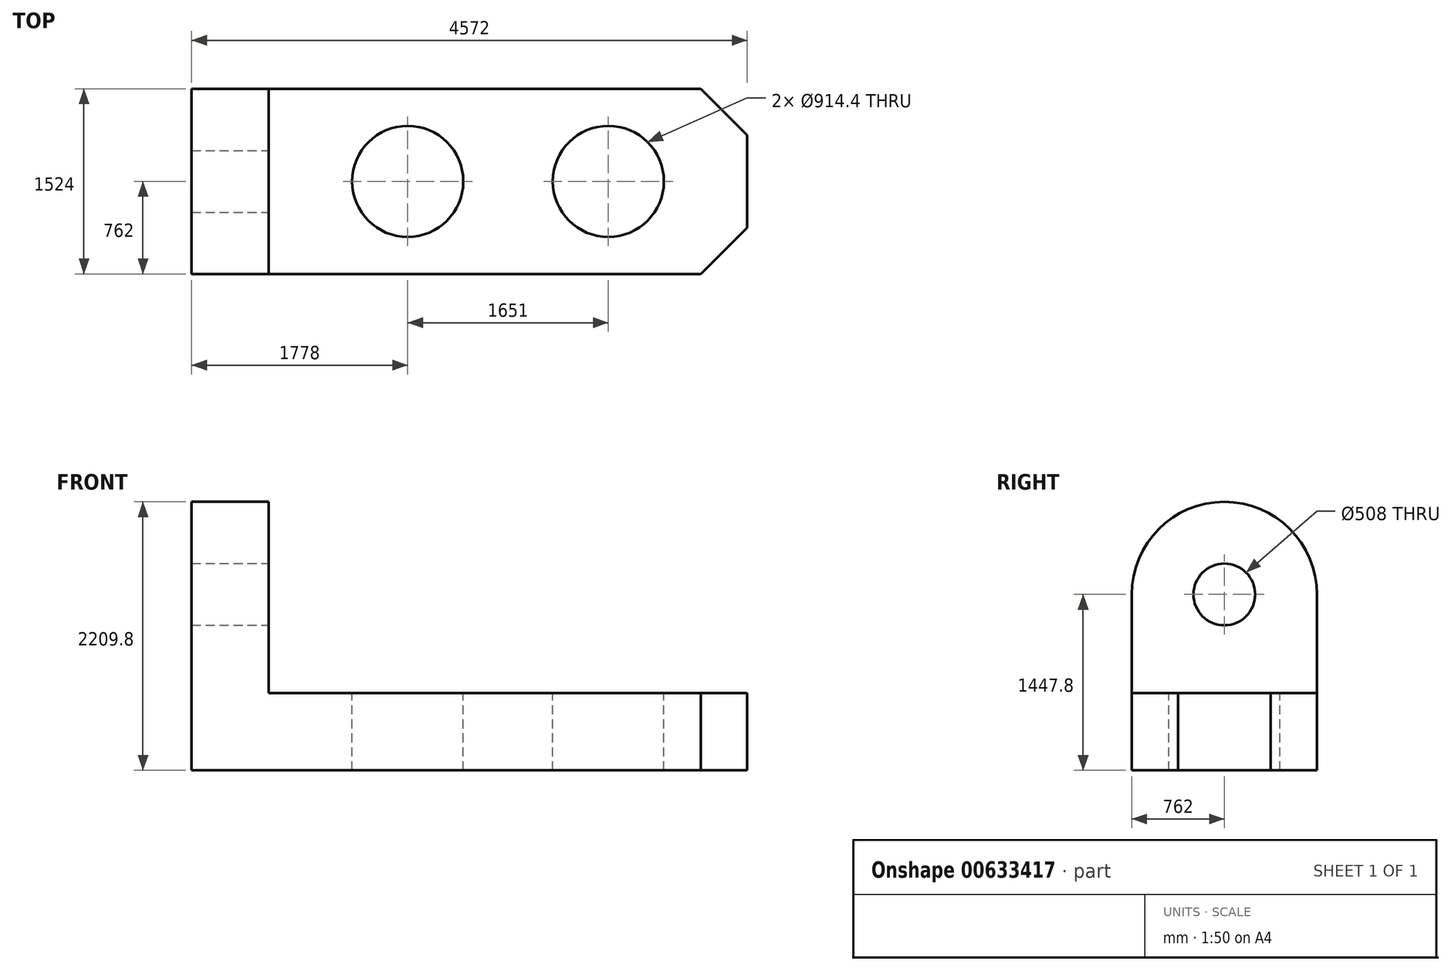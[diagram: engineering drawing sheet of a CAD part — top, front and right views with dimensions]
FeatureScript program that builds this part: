
annotation { "Feature Type Name" : "Feature", "Feature Type Description" : "" }
export const myFeature = defineFeature(function(context is Context, id is Id, definition is map)
    precondition{}
    {
        {
            var Q0;
            Q0=qCreatedBy(makeId("Top.planeOp"),FACE);
            var sketch = newSketch(context, id + "F0", { "sketchPlane" : qUnion([Q0])});
            skLineSegment(sketch, "E0.bottom", {"start": v(0, 0) * mm, "end": v(4572, 0) * mm});
            skLineSegment(sketch, "E0.top", {"start": v(0, 1524) * mm, "end": v(4572, 1524) * mm});
            skLineSegment(sketch, "E0.left", {"start": v(0, 0) * mm, "end": v(0, 1524) * mm});
            skLineSegment(sketch, "E0.right", {"start": v(4572, 0) * mm, "end": v(4572, 1524) * mm});
            skSolve(sketch);
        }
        {
            var Q0;
            Q0=makeQuery(id+"F0.imprint","IMPRINT",FACE,{"disambiguationData":[TD([[makeQuery(id+"F0.imprint","IMPRINT",EDGE,{"derivedFrom":sQuery(id+"F0.wireOp",EDGE,"E0.bottom")}),1.0]])]});
            extrude(context, id + "F1", {"entities" : qUnion([Q0]), "depth" : 635 * mm, "offsetDistance" : 25.4 * mm});
        }
        {
            var Q0;
            Q0=makeQuery(id+"F1.opExtrude","CAP_FACE",FACE,{"disambiguationData":[OSD([sQuery(id+"F0.wireOp",EDGE,"E0.bottom"),sQuery(id+"F0.wireOp",EDGE,"E0.top"),sQuery(id+"F0.wireOp",EDGE,"E0.left"),sQuery(id+"F0.wireOp",EDGE,"E0.right")])],"isStart":false});
            var sketch = newSketch(context, id + "F2", { "sketchPlane" : qUnion([Q0])});
            skLineSegment(sketch, "E1.bottom", {"start": v(0, 0) * mm, "end": v(635, 0) * mm});
            skLineSegment(sketch, "E1.top", {"start": v(0, 1524) * mm, "end": v(635, 1524) * mm});
            skLineSegment(sketch, "E1.left", {"start": v(0, 0) * mm, "end": v(0, 1524) * mm});
            skLineSegment(sketch, "E1.right", {"start": v(635, 0) * mm, "end": v(635, 1524) * mm});
            skSolve(sketch);
        }
        {
            var Q0;
            Q0=makeQuery(id+"F2.imprint","IMPRINT",FACE,{"disambiguationData":[TD([[makeQuery(id+"F2.imprint","IMPRINT",EDGE,{"derivedFrom":sQuery(id+"F2.wireOp",EDGE,"E1.bottom")}),1.0]])]});
            extrude(context, id + "F3", {"entities" : qUnion([Q0]), "operationType" : NewBodyOperationType.ADD, "depth" : 1574.8 * mm, "offsetDistance" : 25.4 * mm});
        }
        {
            var Q0;
            Q0=makeQuery(id+"F3.opExtrude","CAP_EDGE",EDGE,{"disambiguationData":[OSD([sQuery(id+"F2.wireOp",EDGE,"E1.bottom")])],"isStart":false});
            var Q1;
            Q1=makeQuery(id+"F3.opExtrude","CAP_EDGE",EDGE,{"disambiguationData":[OSD([sQuery(id+"F2.wireOp",EDGE,"E1.top")])],"isStart":false});
            fillet(context, id + "F4", {"entities" : qUnion([Q0, Q1]), "radius" : 762 * mm, "tangentPropagation" : true, "allowEdgeOverflow" : false});
        }
        {
            var Q0;
            Q0=makeQuery(id+"F1.opExtrude","CAP_FACE",FACE,{"disambiguationData":[OSD([sQuery(id+"F0.wireOp",EDGE,"E0.bottom"),sQuery(id+"F0.wireOp",EDGE,"E0.top"),sQuery(id+"F0.wireOp",EDGE,"E0.left"),sQuery(id+"F0.wireOp",EDGE,"E0.right")])],"isStart":false});
            var sketch = newSketch(context, id + "F5", { "sketchPlane" : qUnion([Q0])});
            skCircle(sketch, "E2", {"center": v(1778, 762) * mm, "radius": 457.2 * mm});
            skCircle(sketch, "E3", {"center": v(3429, 762) * mm, "radius": 457.2 * mm});
            skSolve(sketch);
        }
        {
            var Q0;
            Q0=makeQuery(id+"F5.imprint","IMPRINT",FACE,{"disambiguationData":[TD([[makeQuery(id+"F5.imprint","IMPRINT",EDGE,{"derivedFrom":sQuery(id+"F5.wireOp",EDGE,"E2")}),1.0]])]});
            var Q1;
            Q1=makeQuery(id+"F5.imprint","IMPRINT",FACE,{"disambiguationData":[TD([[makeQuery(id+"F5.imprint","IMPRINT",EDGE,{"derivedFrom":sQuery(id+"F5.wireOp",EDGE,"E3")}),1.0]])]});
            extrude(context, id + "F6", {"entities" : qUnion([Q0, Q1]), "operationType" : NewBodyOperationType.REMOVE, "oppositeDirection" : true, "depth" : 2540 * mm, "offsetDistance" : 25.4 * mm});
        }
        {
            var Q0;
            Q0=makeQuery(id+"F3.opExtrude","SWEPT_FACE",FACE,{"disambiguationData":[OSD([sQuery(id+"F2.wireOp",EDGE,"E1.right")])]});
            var sketch = newSketch(context, id + "F7", { "sketchPlane" : qUnion([Q0])});
            skCircle(sketch, "E4", {"center": v(762, 1447.8) * mm, "radius": 254 * mm});
            skSolve(sketch);
        }
        {
            var Q0;
            Q0=makeQuery(id+"F7.imprint","IMPRINT",FACE,{"disambiguationData":[TD([[makeQuery(id+"F7.imprint","IMPRINT",EDGE,{"derivedFrom":sQuery(id+"F7.wireOp",EDGE,"E4")}),1.0]])]});
            extrude(context, id + "F8", {"entities" : qUnion([Q0]), "operationType" : NewBodyOperationType.REMOVE, "endBound" : BoundingType.UP_TO_NEXT, "oppositeDirection" : true, "depth" : 25.4 * mm, "offsetDistance" : 25.4 * mm});
        }
        {
            var Q0;
            Q0=makeQuery(id+"F1.opExtrude","SWEPT_EDGE",EDGE,{"disambiguationData":[OSD([sQuery(id+"F0.wireOp",EDGE,"E0.bottom"),sQuery(id+"F0.wireOp",EDGE,"E0.right")])]});
            var Q1;
            Q1=makeQuery(id+"F1.opExtrude","SWEPT_EDGE",EDGE,{"disambiguationData":[OSD([sQuery(id+"F0.wireOp",EDGE,"E0.top"),sQuery(id+"F0.wireOp",EDGE,"E0.right")])]});
            chamfer(context, id + "F9", {"entities" : qUnion([Q0, Q1]), "width" : 381 * mm, "tangentPropagation" : true});
        }
    });
